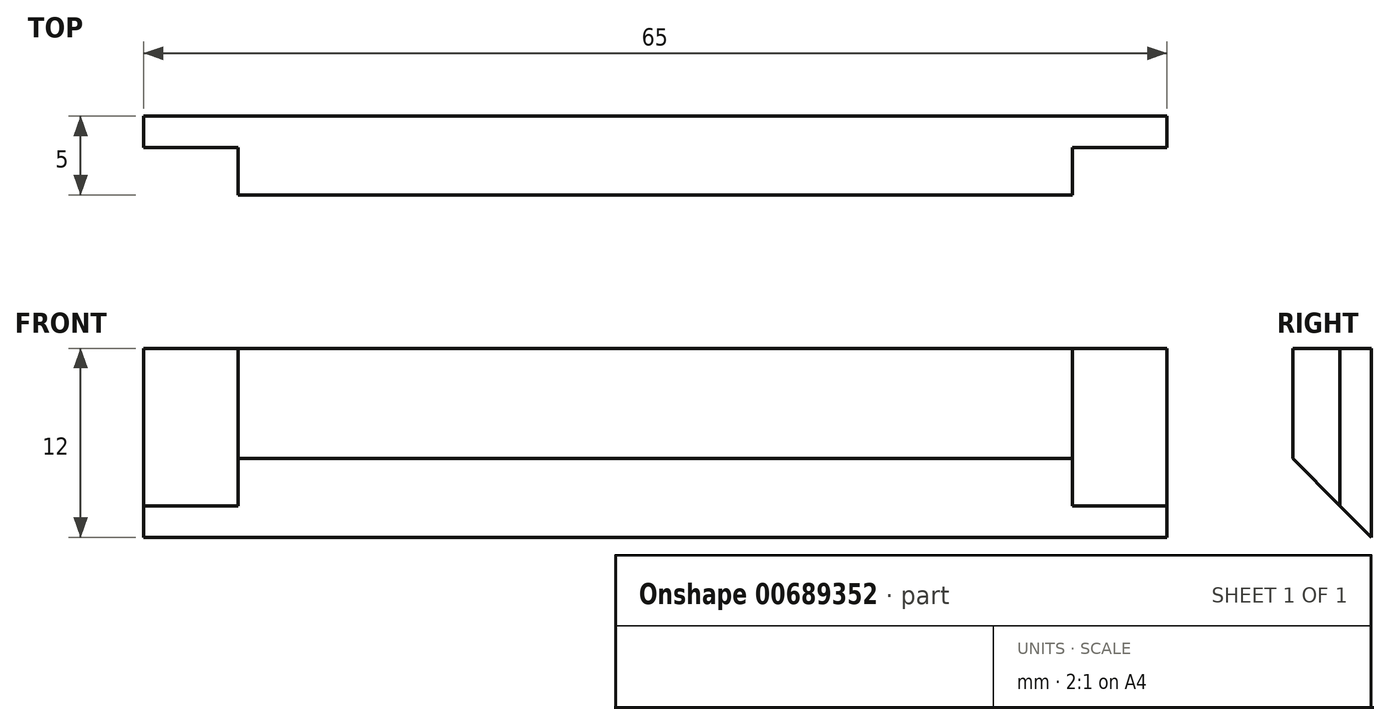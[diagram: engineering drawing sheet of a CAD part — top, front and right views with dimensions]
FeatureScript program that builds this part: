
annotation { "Feature Type Name" : "Feature", "Feature Type Description" : "" }
export const myFeature = defineFeature(function(context is Context, id is Id, definition is map)
    precondition{}
    {
        {
            var Q0;
            Q0=qCreatedBy(makeId("Front.planeOp"),FACE);
            var sketch = newSketch(context, id + "F0", { "sketchPlane" : qUnion([Q0])});
            skLineSegment(sketch, "E0.bottom", {"start": v(32.5, 6) * mm, "end": v(-32.5, 6) * mm});
            skLineSegment(sketch, "E0.top", {"start": v(32.5, -6) * mm, "end": v(-32.5, -6) * mm});
            skLineSegment(sketch, "E0.left", {"start": v(32.5, 6) * mm, "end": v(32.5, -6) * mm});
            skLineSegment(sketch, "E0.right", {"start": v(-32.5, 6) * mm, "end": v(-32.5, -6) * mm});
            skPoint(sketch, "E0.middle", {"position": v(0, 0) * mm});
            skSolve(sketch);
        }
        {
            var Q0;
            Q0=qSketchRegion(id+"F0",true);
            extrude(context, id + "F1", {"entities" : qUnion([Q0]), "oppositeDirection" : true, "depth" : 5 * mm, "offsetDistance" : 25 * mm});
        }
        {
            var Q0;
            Q0=makeQuery(id+"F1.opExtrude","SWEPT_FACE",FACE,{"disambiguationData":[OSD([sQuery(id+"F0.wireOp",EDGE,"E0.right")])]});
            var sketch = newSketch(context, id + "F2", { "sketchPlane" : qUnion([Q0])});
            skLineSegment(sketch, "E1.0", {"start": v(0, -1) * mm, "end": v(0, -6) * mm});
            skLineSegment(sketch, "E2.0", {"start": v(-5, -6) * mm, "end": v(0, -6) * mm});
            skLineSegment(sketch, "E3", {"start": v(-5, -6) * mm, "end": v(0, -1) * mm});
            skPoint(sketch, "E4.orphan", {"position": v(0, 6) * mm});
            skSolve(sketch);
        }
        {
            var Q0;
            Q0=qSketchRegion(id+"F2",true);
            extrude(context, id + "F3", {"entities" : qUnion([Q0]), "operationType" : NewBodyOperationType.REMOVE, "endBound" : BoundingType.THROUGH_ALL, "oppositeDirection" : true, "depth" : 25 * mm, "offsetDistance" : 25 * mm});
        }
        {
            var Q0;
            Q0=makeQuery(id+"F1.opExtrude","CAP_FACE",FACE,{"disambiguationData":[OSD([sQuery(id+"F0.wireOp",EDGE,"E0.bottom"),sQuery(id+"F0.wireOp",EDGE,"E0.top"),sQuery(id+"F0.wireOp",EDGE,"E0.left"),sQuery(id+"F0.wireOp",EDGE,"E0.right")])],"isStart":true});
            var sketch = newSketch(context, id + "F4", { "sketchPlane" : qUnion([Q0])});
            skLineSegment(sketch, "E5.0", {"start": v(32.5, 6) * mm, "end": v(26.5, 6) * mm});
            skLineSegment(sketch, "E6.0", {"start": v(-32.5, 6) * mm, "end": v(-32.5, -6) * mm});
            skLineSegment(sketch, "E7.0", {"start": v(32.5, 6) * mm, "end": v(32.5, -6) * mm});
            skLineSegment(sketch, "E8", {"start": v(-32.5, -6) * mm, "end": v(-26.5, -6) * mm});
            skLineSegment(sketch, "E9", {"start": v(-26.5, 6) * mm, "end": v(-26.5, -6) * mm});
            skLineSegment(sketch, "E10", {"start": v(26.5, 6) * mm, "end": v(26.5, -6) * mm});
            skLineSegment(sketch, "E11.trimOffspring", {"start": v(-26.5, 6) * mm, "end": v(-32.5, 6) * mm});
            skLineSegment(sketch, "E12.trimOffspring", {"start": v(26.5, -6) * mm, "end": v(32.5, -6) * mm});
            skSolve(sketch);
        }
        {
            var Q0;
            Q0=qSketchRegion(id+"F4",true);
            extrude(context, id + "F5", {"entities" : qUnion([Q0]), "operationType" : NewBodyOperationType.REMOVE, "oppositeDirection" : true, "depth" : 3 * mm, "offsetDistance" : 25 * mm});
        }
    });
